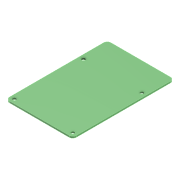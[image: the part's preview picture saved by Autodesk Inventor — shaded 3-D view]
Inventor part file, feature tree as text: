
AUTODESK INVENTOR PART (.ipt)
format: ipt  version: 2022 (Build 260153000, 153)  size: 105,472 bytes
history: native  units: mm
features: sketch x2, extrude x1, fillet x1, hole x1
ambient origin geometry x8: Origin, YZ Plane, XZ Plane, XY Plane, X Axis, Y Axis, Z Axis, Center Point
bodies: Solid1 (feature_tree)
feature tree (5):
  extrude  "Extrusion1"  Depth=56.0mm
  fillet  "Fillet1"  Radius=1.4mm
  hole  "Hole1"  [1 undecoded]
  sketch  "Sketch1"  dims[d0=85.0mm d1=56.0mm d2=1.4mm d3=0.0mm]
  sketch  "Sketch2"  dims[d4=3.0mm d5=49.0mm d6=58.0mm d7=3.5mm d8=3.5mm d9=3.0mm d10=6.0mm d11=4.0mm d12=2.0mm d13=90.0deg d14=6.0mm d15=0.0mm]
note: 1 required parameter value undecoded (feature->parameter linkage not recoverable at this tier; creation-order binding heuristic only, values carry confidence <= 0.55)
